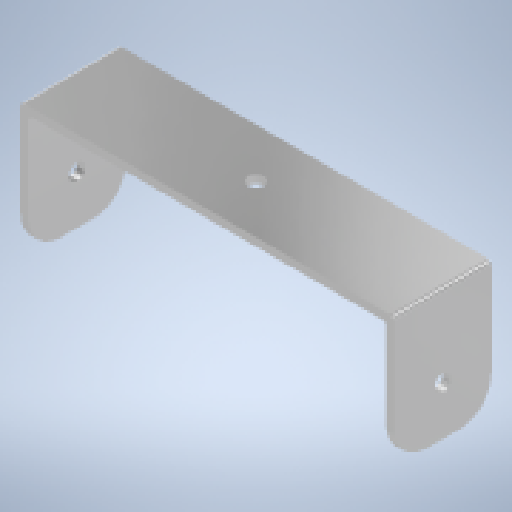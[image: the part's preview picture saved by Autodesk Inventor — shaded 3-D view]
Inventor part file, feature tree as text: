
AUTODESK INVENTOR PART (.ipt)
format: ipt  version: 2024 (Build 280153000, 153)  size: 267,264 bytes
history: native  units: in
note: dims shown in document units (in); Inventor stores cm internally (conversion verified against a paired STEP export)
features: extrude x3, sketch x3, fillet x2
ambient origin geometry x8: Origin, YZ Plane, XZ Plane, XY Plane, X Axis, Y Axis, Z Axis, Center Point
bodies: Body1 (feature_tree)
feature tree (8):
  extrude  "Extrusion4"  Depth=3.0in
  extrude  "Extrusion5"  Depth=4.0in
  fillet  "Fillet4"  Radius=4.0in
  extrude  "Extrusion6"  Depth=0.25in
  fillet  "Fillet5"  Radius=0.25in
  sketch  "Sketch1"  dims[d0=11.5in d1=3.0in]
  sketch  "Sketch4"  dims[d27=0.5in d28=1.5in d30=4.0in d31=0.0in]
  sketch  "Sketch5"  dims[d32=0.25in d33=0.25in d34=0.25in d35=4.6875in d36=0.0in d37=1.0in d38=0.5in d39=2.5in d40=1.5in d41=13.0in d42=0.0in d43=5.75in d44=0.125in d45=5.75in d46=5.75in]
